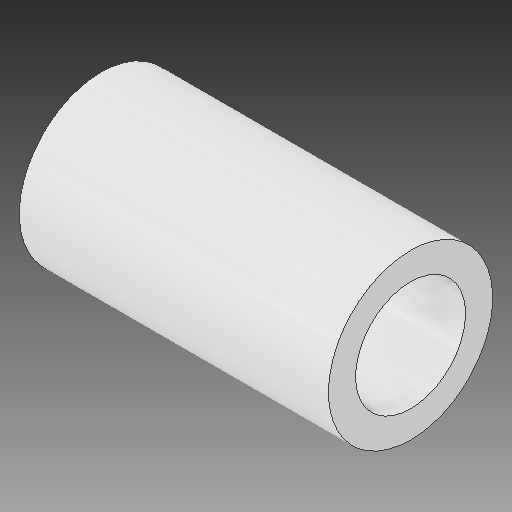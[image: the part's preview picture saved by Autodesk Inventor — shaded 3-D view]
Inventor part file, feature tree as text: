
AUTODESK INVENTOR PART (.ipt)
format: ipt  version: 2017.3 (Build 213256000, 256)  size: 107,008 bytes
history: native  units: mm
features: extrude x1, sketch x1
ambient origin geometry x8: Origin, YZ Plane, XZ Plane, XY Plane, X Axis, Y Axis, Z Axis, Center Point
bodies: Body1 (feature_tree)
feature tree (2):
  extrude  "Extrusion3"  Depth=4.5mm
  sketch  "Sketch4"  dims[d12=2.39mm d13=1.6mm d14=4.5mm d15=0.0mm]
